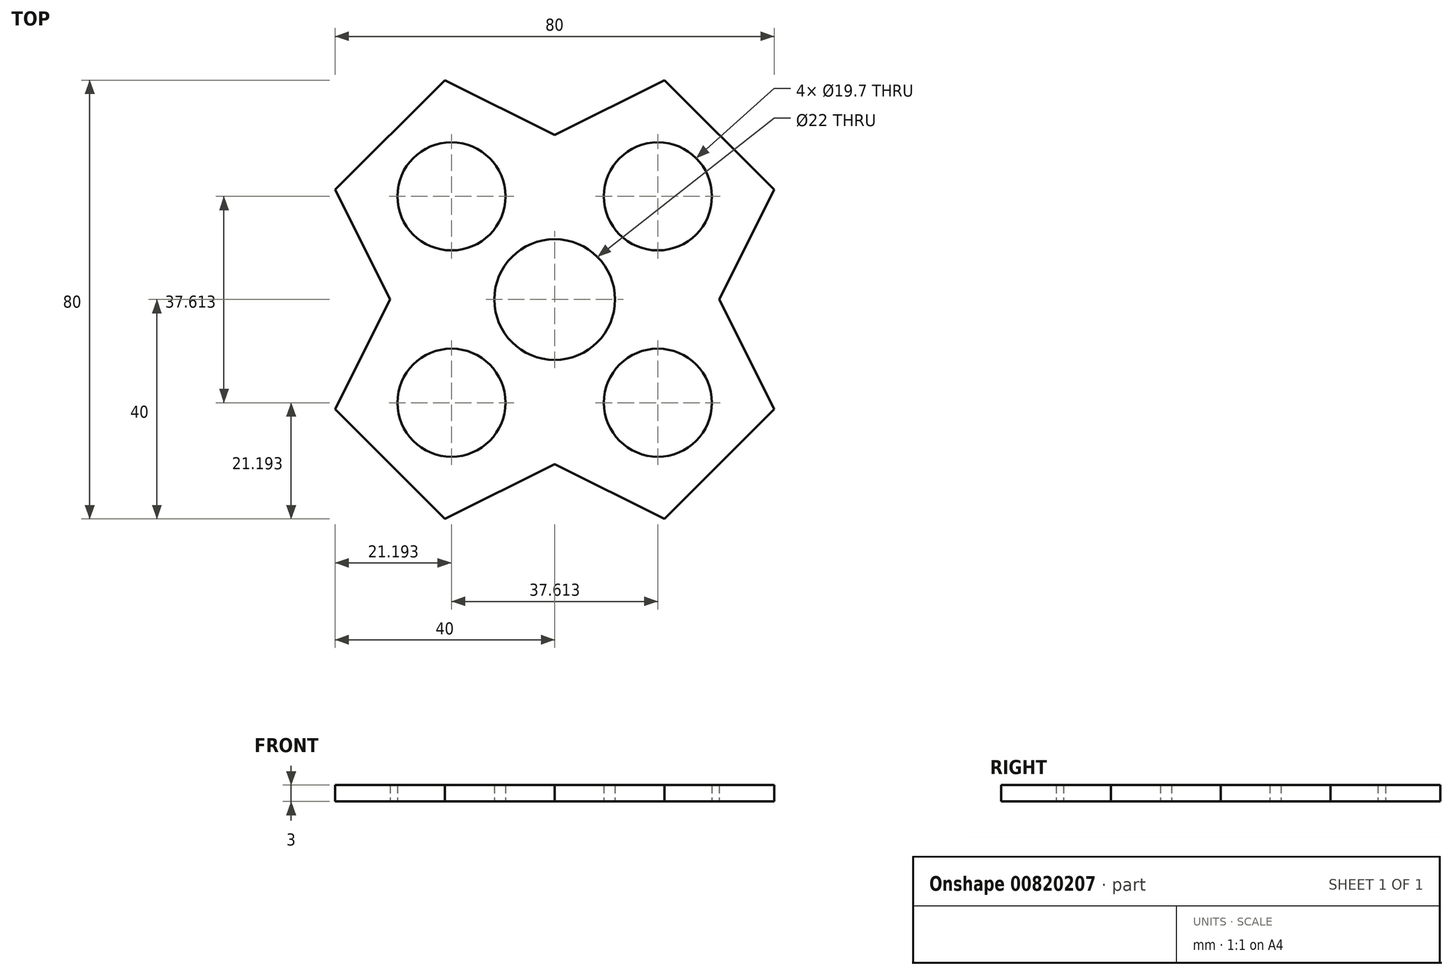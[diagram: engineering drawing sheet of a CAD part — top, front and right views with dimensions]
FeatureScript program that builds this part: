
annotation { "Feature Type Name" : "Feature", "Feature Type Description" : "" }
export const myFeature = defineFeature(function(context is Context, id is Id, definition is map)
    precondition{}
    {
        {
            var Q0;
            Q0=qCreatedBy(makeId("Top.planeOp"),FACE);
            var sketch = newSketch(context, id + "F0", { "sketchPlane" : qUnion([Q0])});
            skCircle(sketch, "E0", {"center": v(0, 0) * mm, "radius": 11 * mm});
            skLineSegment(sketch, "E1", {"start": v(-20, 40) * mm, "end": v(-40, 20) * mm});
            skLineSegment(sketch, "E2", {"start": v(-30, 0) * mm, "end": v(-40, 20) * mm});
            skLineSegment(sketch, "E3", {"start": v(0, 30) * mm, "end": v(-20, 40) * mm});
            skCircle(sketch, "E4", {"center": v(-18.8, 18.8) * mm, "radius": 9.85 * mm});
            skLineSegment(sketch, "E5.1.0", {"start": v(0, -30) * mm, "end": v(-20, -40) * mm});
            skLineSegment(sketch, "E5.1.1", {"start": v(-30, 0) * mm, "end": v(-40, -20) * mm});
            skCircle(sketch, "E5.1.2", {"center": v(-18.8, -18.8) * mm, "radius": 9.85 * mm});
            skLineSegment(sketch, "E5.1.3", {"start": v(-40, -20) * mm, "end": v(-20, -40) * mm});
            skLineSegment(sketch, "E5.2.0", {"start": v(30, 0) * mm, "end": v(40, -20) * mm});
            skLineSegment(sketch, "E5.2.1", {"start": v(0, -30) * mm, "end": v(20, -40) * mm});
            skCircle(sketch, "E5.2.2", {"center": v(18.8, -18.8) * mm, "radius": 9.85 * mm});
            skLineSegment(sketch, "E5.2.3", {"start": v(20, -40) * mm, "end": v(40, -20) * mm});
            skLineSegment(sketch, "E5.3.0", {"start": v(0, 30) * mm, "end": v(20, 40) * mm});
            skLineSegment(sketch, "E5.3.1", {"start": v(30, 0) * mm, "end": v(40, 20) * mm});
            skCircle(sketch, "E5.3.2", {"center": v(18.8, 18.8) * mm, "radius": 9.85 * mm});
            skLineSegment(sketch, "E5.3.3", {"start": v(40, 20) * mm, "end": v(20, 40) * mm});
            skSolve(sketch);
        }
        {
            var Q0;
            Q0=makeQuery(id+"F0.imprint","IMPRINT",FACE,{"disambiguationData":[TD([[makeQuery(id+"F0.imprint","IMPRINT",EDGE,{"derivedFrom":sQuery(id+"F0.wireOp",EDGE,"E1")}),1.0]])]});
            extrude(context, id + "F1", {"entities" : qUnion([Q0]), "depth" : 3 * mm, "offsetDistance" : 25 * mm});
        }
    });
